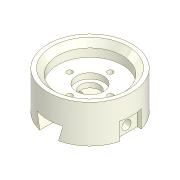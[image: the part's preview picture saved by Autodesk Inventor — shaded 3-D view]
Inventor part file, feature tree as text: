
AUTODESK INVENTOR PART (.ipt)
format: ipt  version: 2022 (Build 260153000, 153)  size: 422,912 bytes
history: native  units: mm
features: sketch x15, extrude x8, hole x6, projected_geometry x5, plane x3, mirror x2, chamfer x2, thicken_offset x1, fillet x1, split x1
ambient origin geometry x8: Origin, YZ Plane, XZ Plane, XY Plane, X Axis, Y Axis, Z Axis, Center Point
bodies: Solid1 (feature_tree), Solid2 (feature_tree), Solid3 (feature_tree)
feature tree (44):
  extrude  "Extrusion1"  Depth=5.0mm TaperAngle=0.0deg
  extrude  "Extrusion2"  Depth=40.0mm TaperAngle=0.0deg
  sketch  "Sketch4"  dims[d9=6.0mm d10=4.0mm d11=2.0mm d12=90.0deg d13=6.0mm d14=0.0mm d15=24.0mm]
  hole  "Hole1"  [1 undecoded]
  mirror  "Mirror1"
  hole  "Hole5"  [1 undecoded]
  thicken_offset  "Thicken1"
  extrude  "Extrusion3"  Depth=5.0mm
  extrude  "Extrusion4"  Depth=2.0mm TaperAngle=45.0deg
  fillet  "Fillet1"  Radius=0.15mm
  hole  "Hole2"  [1 undecoded]
  hole  "Hole3"  [1 undecoded]
  chamfer  "Chamfer1"  Distance=5.0mm
  chamfer  "Chamfer2"  Distance=6.5mm
  plane  "Work Plane1"
  split  "Split1"
  extrude  "Extrusion5"  Depth=9.0mm
  sketch  "Sketch12"  dims[d51=0.15mm]
  plane  "Work Plane2"
  extrude  "Extrusion8"  Depth=5.0mm
  plane  "Work Plane3"
  hole  "Hole9"  [1 undecoded]
  extrude  "Extrusion10"  Depth=15.5mm
  mirror  "Mirror2"
  extrude  "Extrusion11"  Depth=8.0mm
  hole  "Hole10"  [1 undecoded]
  sketch  "Sketch1"  dims[d1=5.0mm d2=24.25mm d3=0.0mm]
  sketch  "Sketch2"  dims[d5=3.0mm d6=40.0mm d7=0.0mm]
  sketch  "Sketch3"  dims[d8=13.0mm]
  sketch  "Sketch5"  dims[d16=5.0mm d17=0.0mm d18=0.0mm d19=0.0mm]
  sketch  "Sketch6"  dims[d20=5.0mm d21=15.0mm]
  sketch  "Sketch7"  dims[d22=40.0mm d24=360.0deg]
  sketch  "Sketch9"  dims[d26=2.0mm d27=6.0mm d28=4.0mm d29=2.0mm d30=90.0deg d31=5.0mm d32=20.594885mm]
  sketch  "Sketch10"  dims[d33=10.0mm d34=6.0mm d35=4.0mm d36=2.0mm d37=90.0deg d38=2.0mm d39=0.0mm d40=2.0mm d41=2.0mm d42=45.0deg d50=0.15mm]
  sketch  "Sketch18"  dims[d52=7.0mm d53=6.0mm d54=4.0mm d55=2.0mm d56=90.0deg d57=6.0mm d58=0.0mm d59=0.5mm d60=2.0mm d61=45.0deg]
  sketch  "Sketch19"  dims[d62=-7.0mm d63=7.0mm]
  sketch  "Sketch22"  dims[d64=7.0mm d65=5.0mm d66=0.0mm]
  sketch  "Sketch24"  dims[d67=14.75mm]
  sketch  "Sketch25"  dims[d68=-14.75mm d97=6.5mm d98=9.0mm d99=5.0mm d100=0.0mm d101=0.0mm d102=15.5mm d104=3.4mm d105=6.0mm d106=4.0mm d107=2.0mm d108=90.0deg d109=8.0mm d110=20.594885mm d117=8.0mm d118=8.0mm d119=2.0mm d120=0.0mm d121=0.2mm d122=0.0mm d123=0.0mm d124=7.0mm d125=6.0mm d126=4.0mm d127=2.0mm d128=90.0deg d129=8.0mm d130=20.594885mm d43=0.15mm d44=0.25mm d45=0.375mm d46=14.3117mm d47=0.75mm d48=20.594885mm d49=0.0625mm]
  projected_geometry  "Project Cut Edges1"
  projected_geometry  "Project Cut Edges2"
  projected_geometry  "Project Cut Edges3"
  projected_geometry  "Project Cut Edges4"
  projected_geometry  "Project Cut Edges5"
note: 6 required parameter values undecoded (feature->parameter linkage not recoverable at this tier; creation-order binding heuristic only, values carry confidence <= 0.55)
